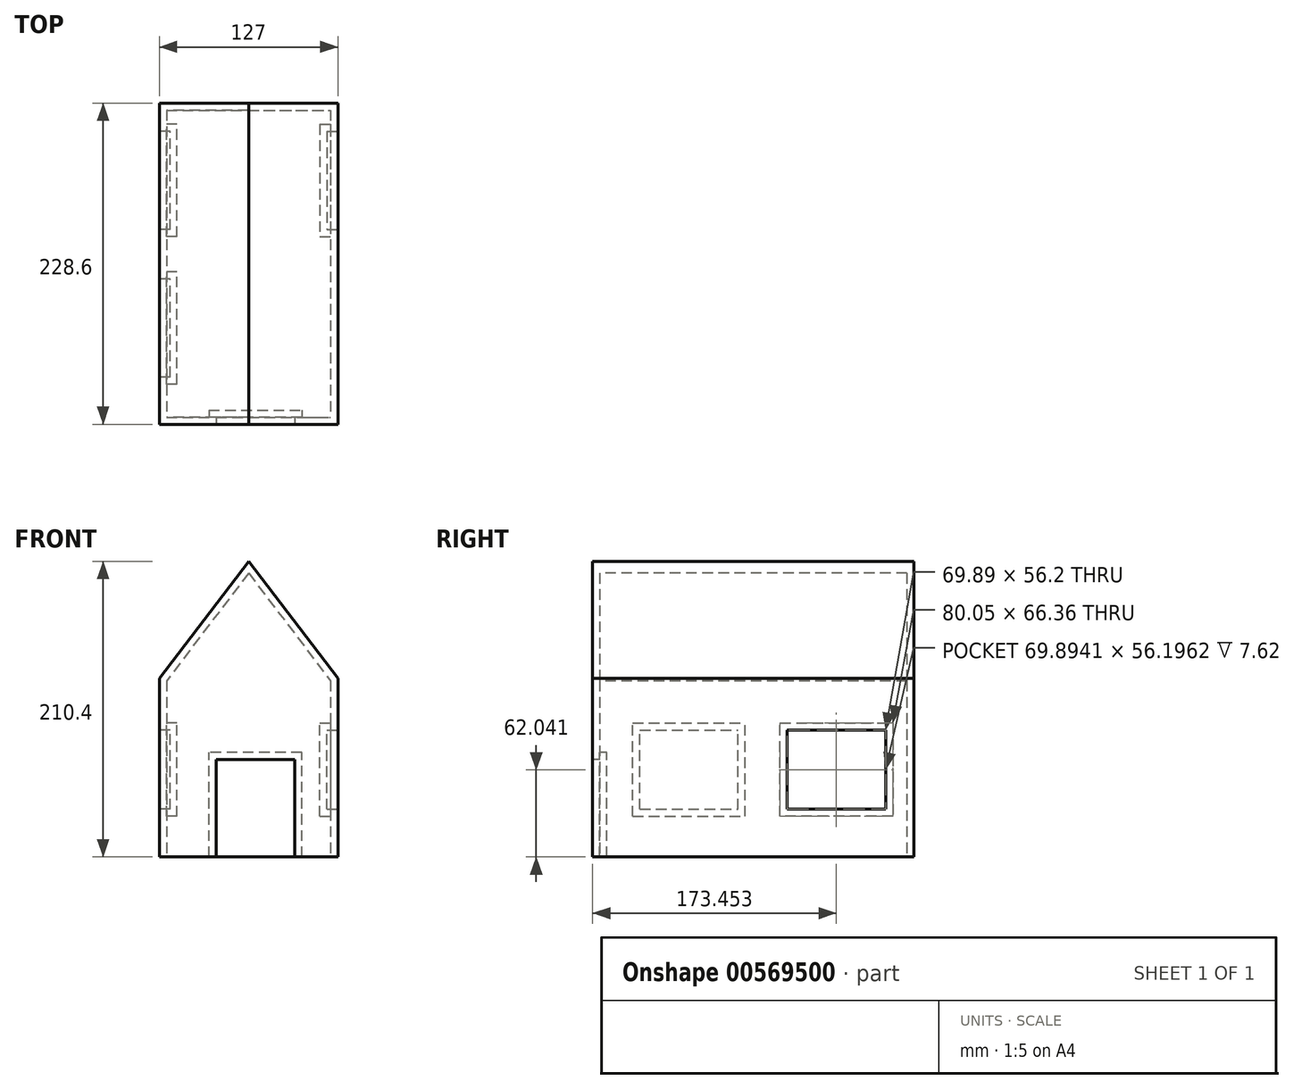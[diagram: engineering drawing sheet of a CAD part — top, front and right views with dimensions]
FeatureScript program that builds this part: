
annotation { "Feature Type Name" : "Feature", "Feature Type Description" : "" }
export const myFeature = defineFeature(function(context is Context, id is Id, definition is map)
    precondition{}
    {
        {
            var Q0;
            Q0=qCreatedBy(makeId("Top.planeOp"),FACE);
            var sketch = newSketch(context, id + "F0", { "sketchPlane" : qUnion([Q0])});
            skLineSegment(sketch, "E0.bottom", {"start": v(0, 0) * mm, "end": v(127, 0) * mm});
            skLineSegment(sketch, "E0.top", {"start": v(0, -127) * mm, "end": v(127, -127) * mm});
            skLineSegment(sketch, "E0.left", {"start": v(0, 0) * mm, "end": v(0, -127) * mm});
            skLineSegment(sketch, "E0.right", {"start": v(127, 0) * mm, "end": v(127, -127) * mm});
            skSolve(sketch);
        }
        {
            var Q0;
            Q0=makeQuery(id+"F0.imprint","IMPRINT",FACE,{"disambiguationData":[TD([[makeQuery(id+"F0.imprint","IMPRINT",EDGE,{"derivedFrom":sQuery(id+"F0.wireOp",EDGE,"E0.bottom")}),-1.0]])]});
            extrude(context, id + "F1", {"entities" : qUnion([Q0]), "depth" : 127 * mm, "offsetDistance" : 25.4 * mm});
        }
        {
            var Q0;
            Q0=makeQuery(id+"F1.opExtrude","SWEPT_FACE",FACE,{"disambiguationData":[OSD([sQuery(id+"F0.wireOp",EDGE,"E0.top")])]});
            extrude(context, id + "F2", {"entities" : qUnion([Q0]), "operationType" : NewBodyOperationType.ADD, "depth" : 25.4 * mm, "offsetDistance" : 25.4 * mm});
        }
        {
            var Q0;
            Q0=makeQuery(id+"F2.opExtrude","CAP_FACE",FACE,{"disambiguationData":[OSD([sQuery(id+"F0.wireOp",EDGE,"E0.top")])],"isStart":false});
            extrude(context, id + "F3", {"entities" : qUnion([Q0]), "operationType" : NewBodyOperationType.ADD, "depth" : 76.2 * mm, "offsetDistance" : 25.4 * mm});
        }
        {
            var Q0;
            Q0=makeQuery(id+"F3.opExtrude","CAP_FACE",FACE,{"disambiguationData":[OSD([sQuery(id+"F0.wireOp",EDGE,"E0.top")])],"isStart":false});
            var sketch = newSketch(context, id + "F4", { "sketchPlane" : qUnion([Q0])});
            skLineSegment(sketch, "E1.0", {"start": v(0, 127) * mm, "end": v(127, 127) * mm});
            skLineSegment(sketch, "E2", {"start": v(63.5, 127) * mm, "end": v(63.5, 210.4) * mm});
            skPoint(sketch, "E2.endSnap0", {"position": v(63.5, 127) * mm});
            skLineSegment(sketch, "E3", {"start": v(63.5, 210.4) * mm, "end": v(127, 127) * mm});
            skLineSegment(sketch, "E4", {"start": v(63.5, 210.4) * mm, "end": v(0, 127) * mm});
            skSolve(sketch);
        }
        {
            var Q0;
            {var subQ2=sQuery(id+"F4.wireOp",EDGE,"E2");Q0=makeQuery(id+"F4.imprint","IMPRINT",FACE,{"disambiguationData":[TD([[makeQuery(id+"F4.imprint","IMPRINT",EDGE,{"derivedFrom":subQ2}),-1.0]])]});}
            var Q1;
            {var subQ2=sQuery(id+"F4.wireOp",EDGE,"E2");Q1=makeQuery(id+"F4.imprint","IMPRINT",FACE,{"disambiguationData":[TD([[makeQuery(id+"F4.imprint","IMPRINT",EDGE,{"derivedFrom":subQ2}),1.0]])]});}
            extrude(context, id + "F5", {"entities" : qUnion([Q0, Q1]), "operationType" : NewBodyOperationType.ADD, "oppositeDirection" : true, "depth" : 228.6 * mm, "offsetDistance" : 25.4 * mm});
        }
        {
            var Q0;
            Q0=makeQuery(id+"F5.boolean.opBoolean","MERGE",FACE,{"derivedFrom":[makeQuery(id+"F3.opExtrude","CAP_FACE",FACE,{"disambiguationData":[OSD([sQuery(id+"F0.wireOp",EDGE,"E0.top")])],"isStart":false}),makeQuery(id+"F5.opExtrude","CAP_FACE",FACE,{"disambiguationData":[OSD([sQuery(id+"F4.wireOp",EDGE,"E1.0"),sQuery(id+"F4.wireOp",EDGE,"E3"),sQuery(id+"F4.wireOp",EDGE,"E4")])],"isStart":true})]});
            var sketch = newSketch(context, id + "F6", { "sketchPlane" : qUnion([Q0])});
            skLineSegment(sketch, "E5.bottom", {"start": v(96.38, 0) * mm, "end": v(40.4, 0) * mm});
            skLineSegment(sketch, "E5.top", {"start": v(96.38, 69.28) * mm, "end": v(40.4, 69.28) * mm});
            skLineSegment(sketch, "E5.left", {"start": v(96.38, 0) * mm, "end": v(96.38, 69.28) * mm});
            skLineSegment(sketch, "E5.right", {"start": v(40.4, 0) * mm, "end": v(40.4, 69.28) * mm});
            skSolve(sketch);
        }
        {
            var Q0;
            Q0 = qSketchRegion(id + "F6", true);
            extrude(context, id + "F7", {"entities" : qUnion([Q0]), "operationType" : NewBodyOperationType.REMOVE, "oppositeDirection" : true, "depth" : 5.08 * mm, "offsetDistance" : 25.4 * mm});
        }
        {
            var Q0;
            {var subQ0=sQuery(id+"F0.wireOp",EDGE,"E0.left");var subQ1=sQuery(id+"F0.wireOp",EDGE,"E0.top");Q0=makeQuery(id+"F3.boolean.opBoolean","MERGE",FACE,{"derivedFrom":[makeQuery(id+"F2.boolean.opBoolean","MERGE",FACE,{"derivedFrom":[makeQuery(id+"F1.opExtrude","SWEPT_FACE",FACE,{"disambiguationData":[OSD([subQ0])]}),makeQuery(id+"F2.opExtrude","SWEPT_FACE",FACE,{"disambiguationData":[OSD([subQ1,subQ0])]})]}),makeQuery(id+"F3.opExtrude","SWEPT_FACE",FACE,{"disambiguationData":[OSD([subQ1,subQ0])]})]});}
            var sketch = newSketch(context, id + "F8", { "sketchPlane" : qUnion([Q0])});
            skLineSegment(sketch, "E6.bottom", {"start": v(90.1, 33.94) * mm, "end": v(20.2, 33.94) * mm});
            skLineSegment(sketch, "E6.top", {"start": v(90.1, 90.14) * mm, "end": v(20.2, 90.14) * mm});
            skLineSegment(sketch, "E6.left", {"start": v(90.1, 33.94) * mm, "end": v(90.1, 90.14) * mm});
            skLineSegment(sketch, "E6.right", {"start": v(20.2, 33.94) * mm, "end": v(20.2, 90.14) * mm});
            skLineSegment(sketch, "E7.1.0.0", {"start": v(195, 90.14) * mm, "end": v(125.1, 90.14) * mm});
            skLineSegment(sketch, "E7.1.0.1", {"start": v(195, 33.94) * mm, "end": v(195, 90.14) * mm});
            skLineSegment(sketch, "E7.1.0.2", {"start": v(195, 33.94) * mm, "end": v(125.1, 33.94) * mm});
            skLineSegment(sketch, "E7.1.0.3", {"start": v(125.1, 33.94) * mm, "end": v(125.1, 90.14) * mm});
            skLineSegment(sketch, "E7.direction1", {"start": v(20.2, 90.14) * mm, "end": v(125.1, 90.14) * mm, "construction": true});
            skSolve(sketch);
        }
        {
            var Q0;
            Q0 = qSketchRegion(id + "F8", true);
            extrude(context, id + "F9", {"entities" : qUnion([Q0]), "operationType" : NewBodyOperationType.REMOVE, "oppositeDirection" : true, "depth" : 7.62 * mm, "offsetDistance" : 25.4 * mm});
        }
        {
            var Q0;
            {var subQ0=sQuery(id+"F0.wireOp",EDGE,"E0.right");var subQ1=sQuery(id+"F0.wireOp",EDGE,"E0.top");Q0=makeQuery(id+"F3.boolean.opBoolean","MERGE",FACE,{"derivedFrom":[makeQuery(id+"F2.boolean.opBoolean","MERGE",FACE,{"derivedFrom":[makeQuery(id+"F1.opExtrude","SWEPT_FACE",FACE,{"disambiguationData":[OSD([subQ0])]}),makeQuery(id+"F2.opExtrude","SWEPT_FACE",FACE,{"disambiguationData":[OSD([subQ1,subQ0])]})]}),makeQuery(id+"F3.opExtrude","SWEPT_FACE",FACE,{"disambiguationData":[OSD([subQ1,subQ0])]})]});}
            var sketch = newSketch(context, id + "F10", { "sketchPlane" : qUnion([Q0])});
            skLineSegment(sketch, "E8.0.0", {"start": v(-90.1, 33.94) * mm, "end": v(-90.1, 90.14) * mm});
            skLineSegment(sketch, "E8.0.1", {"start": v(-90.1, 90.14) * mm, "end": v(-20.2, 90.14) * mm});
            skLineSegment(sketch, "E8.0.2", {"start": v(-20.2, 90.14) * mm, "end": v(-20.2, 33.94) * mm});
            skLineSegment(sketch, "E8.0.3", {"start": v(-20.2, 33.94) * mm, "end": v(-90.1, 33.94) * mm});
            skLineSegment(sketch, "E9.0.0", {"start": v(-125.1, 90.14) * mm, "end": v(-125.1, 33.94) * mm});
            skLineSegment(sketch, "E9.0.1", {"start": v(-125.1, 33.94) * mm, "end": v(-195, 33.94) * mm});
            skLineSegment(sketch, "E9.0.2", {"start": v(-195, 33.94) * mm, "end": v(-195, 90.14) * mm});
            skLineSegment(sketch, "E9.0.3", {"start": v(-195, 90.14) * mm, "end": v(-125.1, 90.14) * mm});
            skSolve(sketch);
        }
        {
            var Q0;
            Q0=makeQuery(id+"F10.imprint","IMPRINT",FACE,{"disambiguationData":[TD([[makeQuery(id+"F10.imprint","IMPRINT",EDGE,{"derivedFrom":sQuery(id+"F10.wireOp",EDGE,"E9.0.0")}),-1.0]])]});
            var sketch = newSketch(context, id + "F11", { "sketchPlane" : qUnion([Q0])});
            skSolve(sketch);
        }
        {
            var Q0;
            Q0=makeQuery(id+"F11.imprint","IMPRINT",FACE,{"disambiguationData":[TD([[makeQuery(id+"F11.imprint","IMPRINT",EDGE,{"derivedFrom":makeQuery(id+"F10.imprint","IMPRINT",EDGE,{"derivedFrom":sQuery(id+"F10.wireOp",EDGE,"E9.0.0")})}),-1.0]])]});
            var Q1;
            Q1=makeQuery(id+"F10.imprint","IMPRINT",FACE,{"disambiguationData":[TD([[makeQuery(id+"F10.imprint","IMPRINT",EDGE,{"derivedFrom":sQuery(id+"F10.wireOp",EDGE,"E8.0.0")}),-1.0]])]});
            extrude(context, id + "F12", {"entities" : qUnion([Q0, Q1]), "operationType" : NewBodyOperationType.REMOVE, "oppositeDirection" : true, "depth" : 7.62 * mm, "offsetDistance" : 25.4 * mm});
        }
        {
            var Q0;
            {var subQ0=sQuery(id+"F0.wireOp",EDGE,"E0.top");var subQ1=makeQuery(id+"F1.opExtrude","CAP_EDGE",EDGE,{"disambiguationData":[OSD([subQ0])],"isStart":true});Q0=makeQuery(id+"F3.boolean.opBoolean","MERGE",FACE,{"derivedFrom":[makeQuery(id+"F2.boolean.opBoolean","MERGE",FACE,{"derivedFrom":[makeQuery(id+"F1.opExtrude","CAP_FACE",FACE,{"disambiguationData":[OSD([sQuery(id+"F0.wireOp",EDGE,"E0.bottom"),subQ0,sQuery(id+"F0.wireOp",EDGE,"E0.left"),sQuery(id+"F0.wireOp",EDGE,"E0.right")])],"isStart":true}),makeQuery(id+"F2.opExtrude","SWEPT_FACE",FACE,{"disambiguationData":[OSD([subQ0]),TDD([subQ1])]})]}),makeQuery(id+"F3.opExtrude","SWEPT_FACE",FACE,{"disambiguationData":[OSD([subQ0]),TDD([makeQuery(id+"F2.opExtrude","CAP_EDGE",EDGE,{"disambiguationData":[OSD([subQ0]),TDD([subQ1])],"isStart":false})])]})]});}
            shell(context, id + "F13", {"entities" : qUnion([Q0]), "thickness" : 5.08 * mm});
        }
    });
